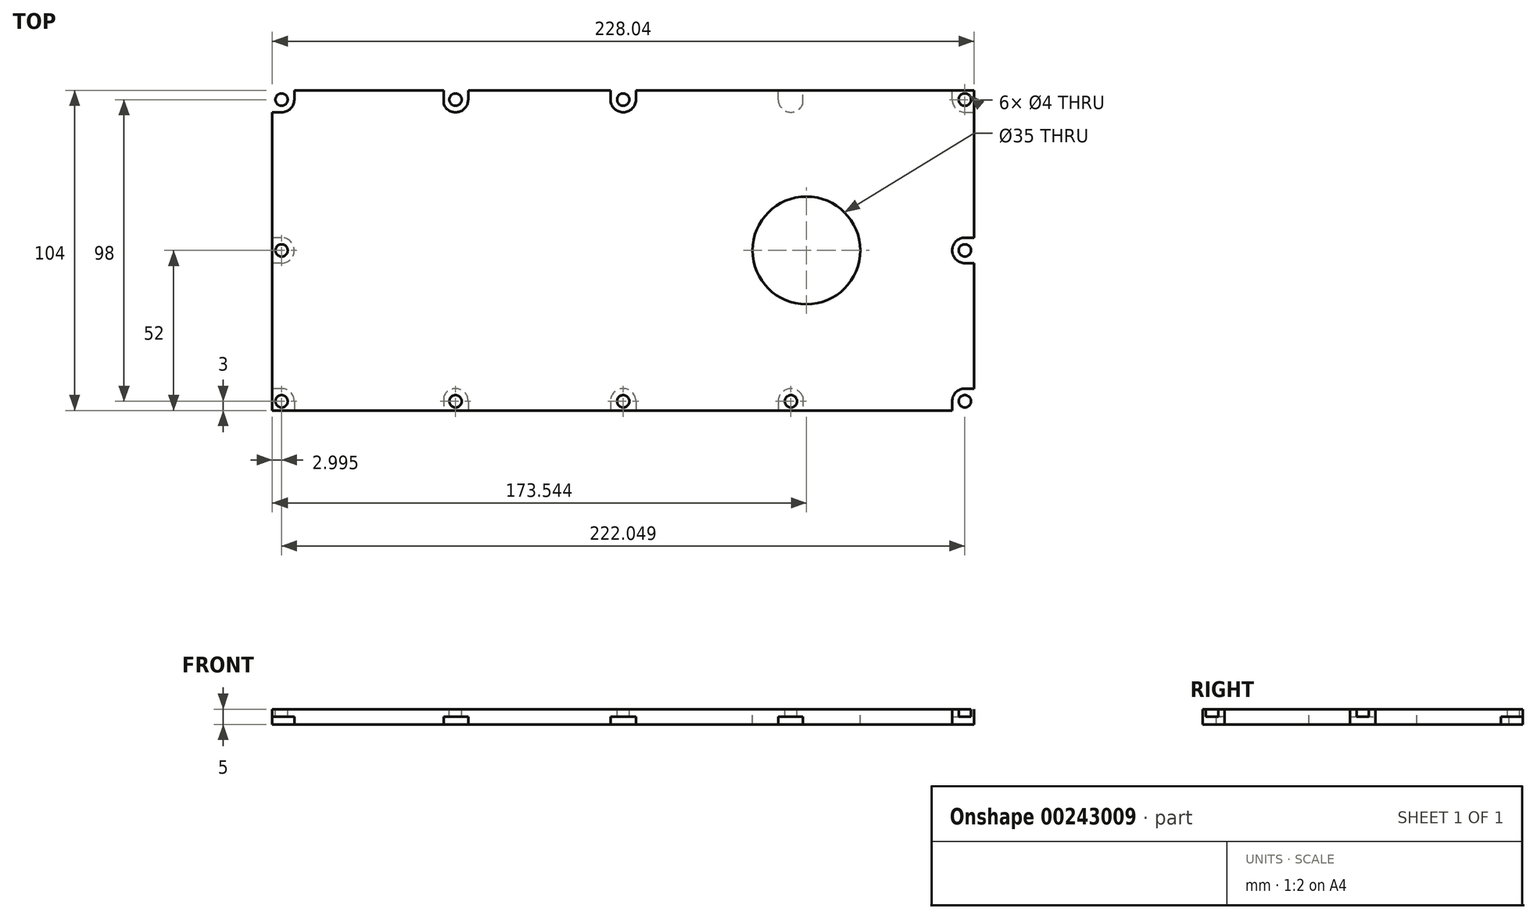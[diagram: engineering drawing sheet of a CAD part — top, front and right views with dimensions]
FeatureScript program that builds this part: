
annotation { "Feature Type Name" : "Feature", "Feature Type Description" : "" }
export const myFeature = defineFeature(function(context is Context, id is Id, definition is map)
    precondition{}
    {
        {
            var Q0;
            Q0=qCreatedBy(makeId("Top.planeOp"),FACE);
            var sketch = newSketch(context, id + "F0", { "sketchPlane" : qUnion([Q0])});
            skLineSegment(sketch, "E0.bottom", {"start": v(-114.02, 52) * mm, "end": v(114.02, 52) * mm});
            skLineSegment(sketch, "E0.top", {"start": v(-114.02, -52) * mm, "end": v(114.02, -52) * mm});
            skLineSegment(sketch, "E0.left", {"start": v(-114.02, 52) * mm, "end": v(-114.02, -52) * mm});
            skLineSegment(sketch, "E0.right", {"start": v(114.02, 52) * mm, "end": v(114.02, -52) * mm});
            skPoint(sketch, "E1", {"position": v(0, 52) * mm});
            skPoint(sketch, "E2", {"position": v(-114.02, 0) * mm});
            skPoint(sketch, "E3", {"position": v(59.52, 0) * mm});
            skCircle(sketch, "E4", {"center": v(59.52, 0) * mm, "radius": 23.5 * mm});
            skCircle(sketch, "E5", {"center": v(59.52, 0) * mm, "radius": 17.5 * mm});
            skLineSegment(sketch, "E6", {"start": v(-111.02, 69.97) * mm, "end": v(-111.02, -88.42) * mm, "construction": true});
            skLineSegment(sketch, "E7", {"start": v(-112.08, -49) * mm, "end": v(189.37, -49) * mm, "construction": true});
            skCircle(sketch, "E8", {"center": v(-111.02, 0) * mm, "radius": 2 * mm});
            skCircle(sketch, "E9", {"center": v(-111.02, -49) * mm, "radius": 2 * mm});
            skCircle(sketch, "E10", {"center": v(-54.5, -49) * mm, "radius": 2 * mm});
            skCircle(sketch, "E11", {"center": v(0, -49) * mm, "radius": 2 * mm});
            skCircle(sketch, "E12", {"center": v(54.5, -49) * mm, "radius": 2 * mm});
            skArc(sketch, "E13", {"start": v(58.38, -47.6) * mm, "mid": v(53.78, -44.94) * mm, "end": v(50.38, -49) * mm});
            skArc(sketch, "E14", {"start": v(4.12, -49) * mm, "mid": v(0, -44.88) * mm, "end": v(-4.12, -49) * mm});
            skArc(sketch, "E15", {"start": v(-50.38, -49) * mm, "mid": v(-54.5, -44.88) * mm, "end": v(-58.63, -49) * mm});
            skArc(sketch, "E16", {"start": v(-106.9, -49) * mm, "mid": v(-108.1, -46.08) * mm, "end": v(-111.02, -44.88) * mm});
            skArc(sketch, "E17", {"start": v(-111.02, -4.12) * mm, "mid": v(-106.9, 0) * mm, "end": v(-111.02, 4.12) * mm});
            skCircle(sketch, "E18.MirrorC", {"center": v(54.5, 49) * mm, "radius": 2 * mm});
            skCircle(sketch, "E19.MirrorC", {"center": v(0, 49) * mm, "radius": 2 * mm});
            skCircle(sketch, "E20.MirrorC", {"center": v(-54.5, 49) * mm, "radius": 2 * mm});
            skCircle(sketch, "E21.MirrorC", {"center": v(-111.02, 49) * mm, "radius": 2 * mm});
            skArc(sketch, "E22.MirrorC", {"start": v(-106.9, 49) * mm, "mid": v(-108.1, 46.08) * mm, "end": v(-111.02, 44.88) * mm});
            skArc(sketch, "E23.MirrorC", {"start": v(-50.38, 49) * mm, "mid": v(-53.78, 44.94) * mm, "end": v(-58.38, 47.6) * mm});
            skArc(sketch, "E24.MirrorC", {"start": v(4.12, 49) * mm, "mid": v(0, 44.88) * mm, "end": v(-4.12, 49) * mm});
            skArc(sketch, "E25.MirrorC", {"start": v(58.38, 47.6) * mm, "mid": v(53.78, 44.94) * mm, "end": v(50.38, 49) * mm});
            skCircle(sketch, "E26.MirrorC", {"center": v(111.02, 0) * mm, "radius": 2 * mm});
            skCircle(sketch, "E27.MirrorC", {"center": v(111.02, 49) * mm, "radius": 2 * mm});
            skArc(sketch, "E28.MirrorC", {"start": v(106.9, 49) * mm, "mid": v(108.1, 46.08) * mm, "end": v(111.02, 44.88) * mm});
            skPoint(sketch, "E29.MirrorP", {"position": v(114.02, 0) * mm});
            skArc(sketch, "E30.MirrorC", {"start": v(111.02, -4.12) * mm, "mid": v(106.9, 0) * mm, "end": v(111.02, 4.12) * mm});
            skCircle(sketch, "E31.MirrorC", {"center": v(111.02, -49) * mm, "radius": 2 * mm});
            skArc(sketch, "E32.MirrorC", {"start": v(106.9, -49) * mm, "mid": v(108.1, -46.08) * mm, "end": v(111.02, -44.88) * mm});
            skLineSegment(sketch, "E33", {"start": v(-111.02, 4.12) * mm, "end": v(-114.02, 4.12) * mm});
            skLineSegment(sketch, "E34", {"start": v(-111.02, -4.13) * mm, "end": v(-114.02, -4.13) * mm});
            skLineSegment(sketch, "E35", {"start": v(-106.9, -49) * mm, "end": v(-106.9, -52) * mm});
            skLineSegment(sketch, "E36", {"start": v(-111.02, -44.88) * mm, "end": v(-114.02, -44.88) * mm});
            skLineSegment(sketch, "E37", {"start": v(-58.38, -47.6) * mm, "end": v(-58.38, -52) * mm});
            skLineSegment(sketch, "E38", {"start": v(-50.38, -49) * mm, "end": v(-50.38, -52) * mm});
            skLineSegment(sketch, "E39", {"start": v(-4.13, -49) * mm, "end": v(-4.13, -52) * mm});
            skLineSegment(sketch, "E40", {"start": v(4.12, -49) * mm, "end": v(4.12, -52) * mm});
            skLineSegment(sketch, "E41.MirrorCS", {"start": v(-111.02, 44.88) * mm, "end": v(-114.02, 44.88) * mm});
            skLineSegment(sketch, "E42.MirrorCS", {"start": v(-106.9, 49) * mm, "end": v(-106.9, 52) * mm});
            skLineSegment(sketch, "E43.MirrorCS", {"start": v(-58.38, 47.6) * mm, "end": v(-58.38, 52) * mm});
            skLineSegment(sketch, "E44.MirrorCS", {"start": v(4.13, 49) * mm, "end": v(4.13, 52) * mm});
            skLineSegment(sketch, "E45.MirrorCS", {"start": v(-50.38, 49) * mm, "end": v(-50.38, 52) * mm});
            skLineSegment(sketch, "E46.MirrorCS", {"start": v(-4.13, 49) * mm, "end": v(-4.13, 52) * mm});
            skLineSegment(sketch, "E47.MirrorCS", {"start": v(106.9, 49) * mm, "end": v(106.9, 52) * mm});
            skLineSegment(sketch, "E48.MirrorCS", {"start": v(58.38, 47.6) * mm, "end": v(58.38, 52) * mm});
            skLineSegment(sketch, "E49.MirrorCS", {"start": v(50.38, 49) * mm, "end": v(50.38, 52) * mm});
            skArc(sketch, "E50.MirrorC", {"start": v(50.38, 49) * mm, "mid": v(53.78, 44.94) * mm, "end": v(58.38, 47.6) * mm});
            skLineSegment(sketch, "E51.MirrorCS", {"start": v(114.02, 52) * mm, "end": v(-114.02, 52) * mm});
            skLineSegment(sketch, "E52.MirrorCS", {"start": v(111.02, -44.88) * mm, "end": v(114.02, -44.88) * mm});
            skLineSegment(sketch, "E53.MirrorCS", {"start": v(111.02, -4.12) * mm, "end": v(114.02, -4.12) * mm});
            skLineSegment(sketch, "E54.MirrorCS", {"start": v(111.02, 44.88) * mm, "end": v(114.02, 44.88) * mm});
            skLineSegment(sketch, "E55.MirrorCS", {"start": v(111.02, 4.12) * mm, "end": v(114.02, 4.12) * mm});
            skLineSegment(sketch, "E56.MirrorCS", {"start": v(106.9, -49) * mm, "end": v(106.9, -52) * mm});
            skLineSegment(sketch, "E57.MirrorCS", {"start": v(58.38, -47.6) * mm, "end": v(58.38, -52) * mm});
            skLineSegment(sketch, "E58.MirrorCS", {"start": v(50.38, -49) * mm, "end": v(50.38, -52) * mm});
            skSolve(sketch);
        }
        {
            var Q0;
            Q0=makeQuery(id+"F0.imprint","IMPRINT",FACE,{"disambiguationData":[TD([[makeQuery(id+"F0.imprint","IMPRINT",EDGE,{"derivedFrom":sQuery(id+"F0.wireOp",EDGE,"E0.bottom")}),-1.0]])]});
            var Q1;
            Q1=makeQuery(id+"F0.imprint","IMPRINT",FACE,{"disambiguationData":[TD([[makeQuery(id+"F0.imprint","IMPRINT",EDGE,{"derivedFrom":sQuery(id+"F0.wireOp",EDGE,"4ljCUxYP-cvLy-LUiz-s5sy-Mq0FhNnpUv07")}),1.0]])]});
            var Q2;
            Q2=makeQuery(id+"F0.imprint","IMPRINT",FACE,{"disambiguationData":[TD([[makeQuery(id+"F0.imprint","IMPRINT",EDGE,{"derivedFrom":sQuery(id+"F0.wireOp",EDGE,"E4")}),1.0]])]});
            var Q3;
            Q3=makeQuery(id+"F0.imprint","IMPRINT",FACE,{"disambiguationData":[TD([[makeQuery(id+"F0.imprint","IMPRINT",EDGE,{"derivedFrom":sQuery(id+"F0.wireOp",EDGE,"sXJLWkI9-QaLD-srrT-vsYK-vLixfe091RBh")}),1.0]])]});
            var Q4;
            Q4=makeQuery(id+"F0.imprint","IMPRINT",FACE,{"disambiguationData":[TD([[makeQuery(id+"F0.imprint","IMPRINT",EDGE,{"derivedFrom":sQuery(id+"F0.wireOp",EDGE,"sXJLWkI9-QaLD-srrT-vsYK-vLixfe091RBh")}),-1.0]])]});
            var Q5;
            Q5=makeQuery(id+"F0.imprint","IMPRINT",FACE,{"disambiguationData":[TD([[makeQuery(id+"F0.imprint","IMPRINT",EDGE,{"derivedFrom":sQuery(id+"F0.wireOp",EDGE,"E4")}),-1.0]])]});
            extrude(context, id + "F1", {"entities" : qUnion([Q0, Q1, Q2, Q3, Q4, Q5]), "oppositeDirection" : true, "depth" : 5 * mm});
        }
        {
            var Q0;
            Q0=makeQuery(id+"F0.imprint","IMPRINT",FACE,{"disambiguationData":[TD([[makeQuery(id+"F0.imprint","IMPRINT",EDGE,{"derivedFrom":sQuery(id+"F0.wireOp",EDGE,"E21.MirrorC")}),1.0]])]});
            var Q1;
            Q1=makeQuery(id+"F0.imprint","IMPRINT",FACE,{"disambiguationData":[TD([[makeQuery(id+"F0.imprint","IMPRINT",EDGE,{"derivedFrom":sQuery(id+"F0.wireOp",EDGE,"E8")}),-1.0]])]});
            var Q2;
            Q2=makeQuery(id+"F0.imprint","IMPRINT",FACE,{"disambiguationData":[TD([[makeQuery(id+"F0.imprint","IMPRINT",EDGE,{"derivedFrom":sQuery(id+"F0.wireOp",EDGE,"E9")}),-1.0]])]});
            var Q3;
            Q3=makeQuery(id+"F0.imprint","IMPRINT",FACE,{"disambiguationData":[TD([[makeQuery(id+"F0.imprint","IMPRINT",EDGE,{"derivedFrom":sQuery(id+"F0.wireOp",EDGE,"E10")}),-1.0]])]});
            var Q4;
            Q4=makeQuery(id+"F0.imprint","IMPRINT",FACE,{"disambiguationData":[TD([[makeQuery(id+"F0.imprint","IMPRINT",EDGE,{"derivedFrom":sQuery(id+"F0.wireOp",EDGE,"E11")}),-1.0]])]});
            var Q5;
            Q5=makeQuery(id+"F0.imprint","IMPRINT",FACE,{"disambiguationData":[TD([[makeQuery(id+"F0.imprint","IMPRINT",EDGE,{"derivedFrom":sQuery(id+"F0.wireOp",EDGE,"E12")}),-1.0]])]});
            var Q6;
            Q6=makeQuery(id+"F0.imprint","IMPRINT",FACE,{"disambiguationData":[TD([[makeQuery(id+"F0.imprint","IMPRINT",EDGE,{"derivedFrom":sQuery(id+"F0.wireOp",EDGE,"E31.MirrorC")}),1.0]])]});
            var Q7;
            Q7=makeQuery(id+"F0.imprint","IMPRINT",FACE,{"disambiguationData":[TD([[makeQuery(id+"F0.imprint","IMPRINT",EDGE,{"derivedFrom":sQuery(id+"F0.wireOp",EDGE,"E26.MirrorC")}),1.0]])]});
            var Q8;
            Q8=makeQuery(id+"F0.imprint","IMPRINT",FACE,{"disambiguationData":[TD([[makeQuery(id+"F0.imprint","IMPRINT",EDGE,{"derivedFrom":sQuery(id+"F0.wireOp",EDGE,"E27.MirrorC")}),-1.0]])]});
            var Q9;
            Q9=makeQuery(id+"F0.imprint","IMPRINT",FACE,{"disambiguationData":[TD([[makeQuery(id+"F0.imprint","IMPRINT",EDGE,{"derivedFrom":sQuery(id+"F0.wireOp",EDGE,"E18.MirrorC")}),1.0]])]});
            var Q10;
            Q10=makeQuery(id+"F0.imprint","IMPRINT",FACE,{"disambiguationData":[TD([[makeQuery(id+"F0.imprint","IMPRINT",EDGE,{"derivedFrom":sQuery(id+"F0.wireOp",EDGE,"E19.MirrorC")}),1.0]])]});
            var Q11;
            Q11=makeQuery(id+"F0.imprint","IMPRINT",FACE,{"disambiguationData":[TD([[makeQuery(id+"F0.imprint","IMPRINT",EDGE,{"derivedFrom":sQuery(id+"F0.wireOp",EDGE,"E20.MirrorC")}),1.0]])]});
            var Q12;
            {var subQ1=sQuery(id+"F0.wireOp",EDGE,"E48.MirrorCS");Q12=makeQuery(id+"F0.imprint","IMPRINT",FACE,{"disambiguationData":[TD([[makeQuery(id+"F0.imprint","IMPRINT",EDGE,{"derivedFrom":subQ1}),1.0]])]});}
            extrude(context, id + "F2", {"entities" : qUnion([Q0, Q1, Q2, Q3, Q4, Q5, Q6, Q7, Q8, Q9, Q10, Q11, Q12]), "operationType" : NewBodyOperationType.ADD, "oppositeDirection" : true, "depth" : 2.5 * mm});
        }
    });
